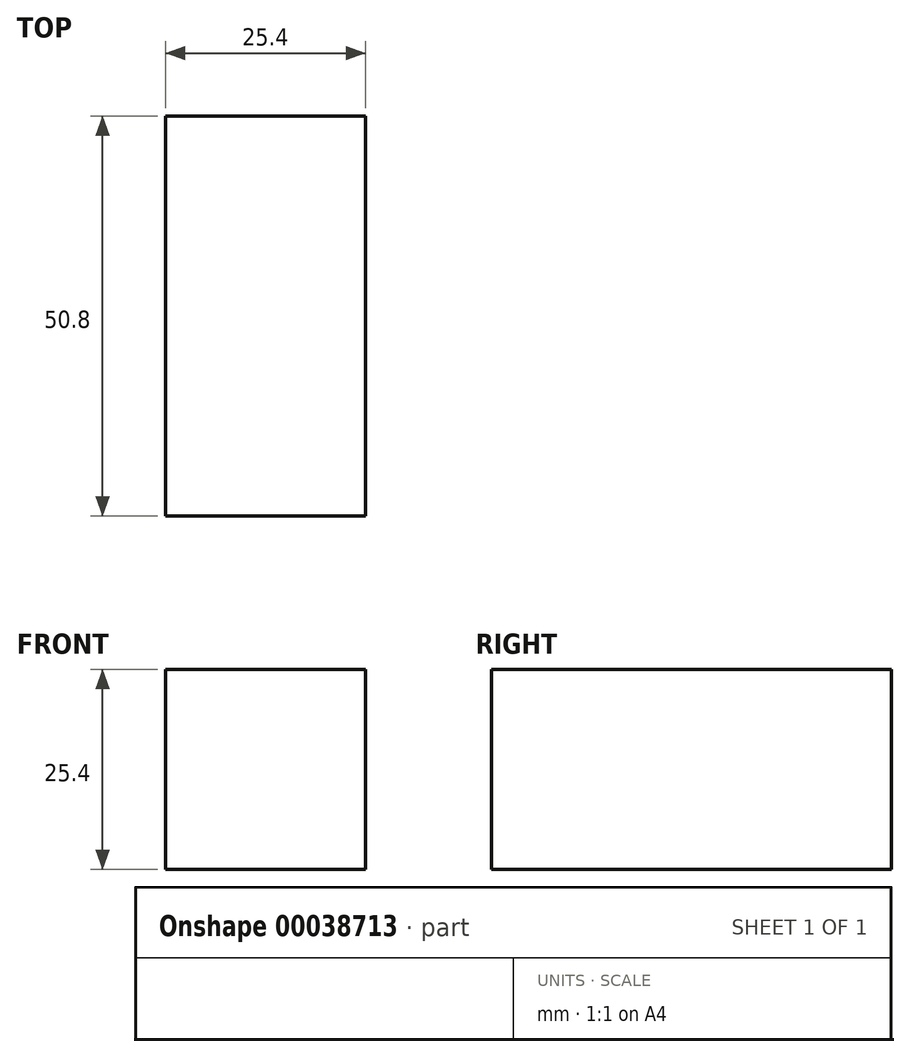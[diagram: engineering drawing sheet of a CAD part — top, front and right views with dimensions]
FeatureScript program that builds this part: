
annotation { "Feature Type Name" : "Feature", "Feature Type Description" : "" }
export const myFeature = defineFeature(function(context is Context, id is Id, definition is map)
    precondition{}
    {
        {
            var Q0;
            Q0=qCreatedBy(makeId("Top.planeOp"),FACE);
            var sketch = newSketch(context, id + "F0", { "sketchPlane" : qUnion([Q0])});
            skLineSegment(sketch, "E0.bottom", {"start": v(-12.26, 0) * mm, "end": v(13.14, 0) * mm});
            skLineSegment(sketch, "E0.top", {"start": v(-12.26, 50.8) * mm, "end": v(13.14, 50.8) * mm});
            skLineSegment(sketch, "E0.left", {"start": v(-12.26, 0) * mm, "end": v(-12.26, 50.8) * mm});
            skLineSegment(sketch, "E0.right", {"start": v(13.14, 0) * mm, "end": v(13.14, 50.8) * mm});
            skSolve(sketch);
        }
        {
            var Q0;
            Q0=qSketchRegion(id+"F0",true);
            extrude(context, id + "F1", {"entities" : qUnion([Q0]), "depth" : 25.4 * mm});
        }
    });
